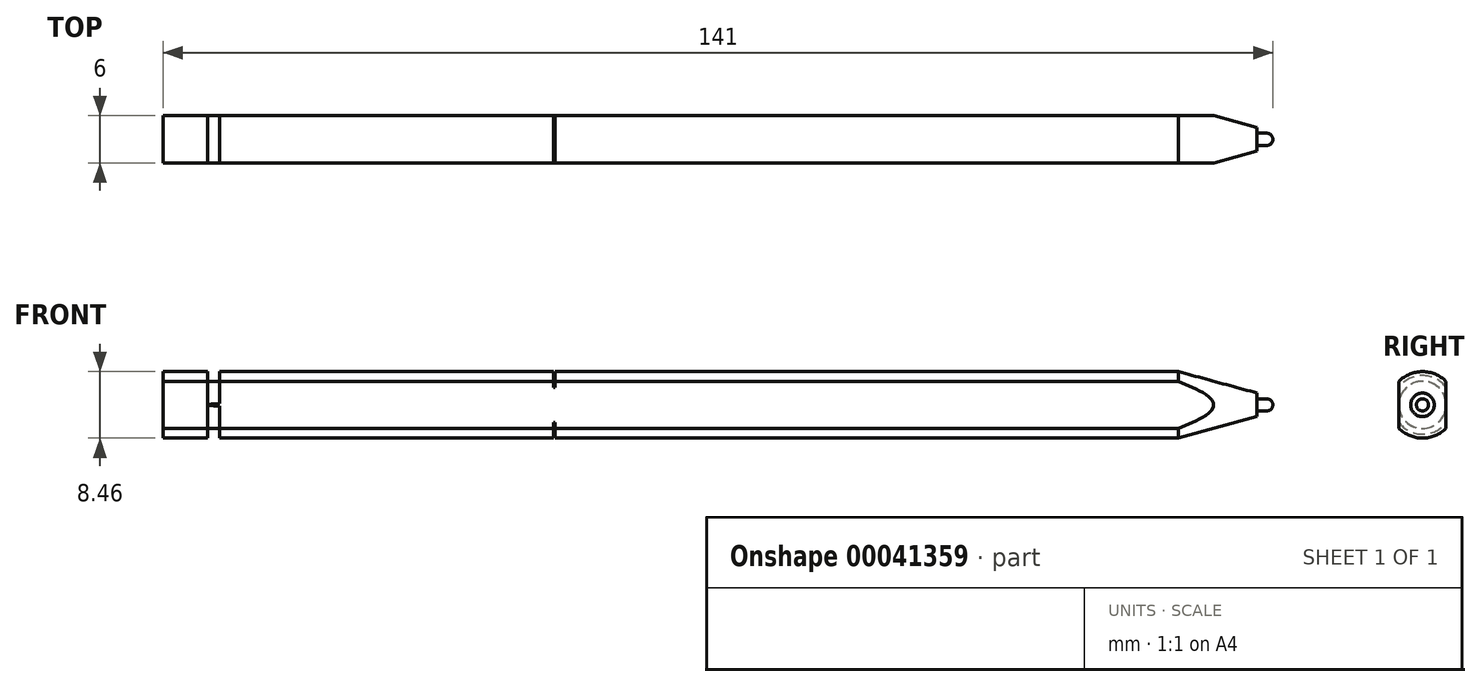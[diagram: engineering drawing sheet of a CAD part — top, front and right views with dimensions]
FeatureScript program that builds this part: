
annotation { "Feature Type Name" : "Feature", "Feature Type Description" : "" }
export const myFeature = defineFeature(function(context is Context, id is Id, definition is map)
    precondition{}
    {
        {
            var Q0;
            Q0=qCreatedBy(makeId("Top.planeOp"),FACE);
            var sketch = newSketch(context, id + "F0", { "sketchPlane" : qUnion([Q0])});
            skLineSegment(sketch, "E0", {"start": v(-68.74, 0) * mm, "end": v(70.26, 0) * mm});
            skLineSegment(sketch, "E1", {"start": v(70.26, 1.5) * mm, "end": v(60.26, 4.22) * mm});
            skLineSegment(sketch, "E2", {"start": v(-63.04, 4.22) * mm, "end": v(-63.04, 3) * mm});
            skLineSegment(sketch, "E3", {"start": v(-63.04, 3) * mm, "end": v(-61.54, 3) * mm});
            skLineSegment(sketch, "E4", {"start": v(-61.54, 3) * mm, "end": v(-61.54, 4.22) * mm});
            skLineSegment(sketch, "E5", {"start": v(-63.04, 4.22) * mm, "end": v(-68.74, 4.22) * mm});
            skLineSegment(sketch, "E6", {"start": v(-68.74, 4.22) * mm, "end": v(-68.74, 0) * mm});
            skLineSegment(sketch, "E7", {"start": v(70.26, 1.5) * mm, "end": v(70.26, 0.78) * mm});
            skPoint(sketch, "E8.orphan", {"position": v(72.26, 0) * mm});
            skLineSegment(sketch, "E9", {"start": v(70.26, 0.78) * mm, "end": v(71.48, 0.78) * mm});
            skArc(sketch, "E10", {"start": v(71.48, 0.78) * mm, "mid": v(72.03, 0.55) * mm, "end": v(72.26, 0) * mm});
            skLineSegment(sketch, "E11", {"start": v(70.26, 0) * mm, "end": v(72.26, 0) * mm});
            skLineSegment(sketch, "E12", {"start": v(-61.54, 4.22) * mm, "end": v(-19.14, 4.22) * mm});
            skLineSegment(sketch, "E13", {"start": v(-18.94, 4.22) * mm, "end": v(-18.94, 3.73) * mm});
            skLineSegment(sketch, "E14", {"start": v(-19.14, 3.73) * mm, "end": v(-18.94, 3.73) * mm});
            skLineSegment(sketch, "E15", {"start": v(-19.14, 3.73) * mm, "end": v(-19.14, 4.22) * mm});
            skLineSegment(sketch, "E16.trimOffspring", {"start": v(-18.94, 4.22) * mm, "end": v(60.26, 4.22) * mm});
            skSolve(sketch);
        }
        {
            var Q0;
            {var subQ0=sQuery(id+"F0.wireOp",EDGE,"E0");Q0=makeQuery(id+"F0.imprint","IMPRINT",FACE,{"disambiguationData":[TD([[makeQuery(id+"F0.imprint","IMPRINT",EDGE,{"derivedFrom":subQ0}),1.0]])]});}
            var Q1;
            Q1=sQuery(id+"F0.wireOp",EDGE,"E0");
            revolve(context, id + "F1", {"entities" : qUnion([Q0]), "axis" : qUnion([Q1]), "revolveType" : RevolveType.FULL});
        }
        {
            var Q0;
            Q0=makeQuery(id+"F1.opRevolve","SWEPT_FACE",FACE,{"disambiguationData":[OSD([sQuery(id+"F0.wireOp",EDGE,"E6")])]});
            var sketch = newSketch(context, id + "F2", { "sketchPlane" : qUnion([Q0])});
            skLineSegment(sketch, "E17.bottom", {"start": v(-3, 4.22) * mm, "end": v(3, 4.22) * mm});
            skLineSegment(sketch, "E17.top", {"start": v(-3, -4.22) * mm, "end": v(3, -4.22) * mm});
            skLineSegment(sketch, "E17.left", {"start": v(-3, 4.22) * mm, "end": v(-3, -4.22) * mm});
            skLineSegment(sketch, "E17.right", {"start": v(3, 4.22) * mm, "end": v(3, -4.22) * mm});
            skSolve(sketch);
        }
        {
            var Q0;
            {var subQ0=makeQuery(id+"F1.opRevolve","SWEPT_EDGE",EDGE,{"disambiguationData":[OSD([sQuery(id+"F0.wireOp",EDGE,"E5"),sQuery(id+"F0.wireOp",EDGE,"E6")])]});var subQ1=sQuery(id+"F2.wireOp",EDGE,"E17.left");var subQ3=makeQuery(id+"F2.imprint","INTERSECT",VERTEX,{"disambiguationData":[OD(0.0)],"derivedFrom":[subQ0,subQ1]});Q0=makeQuery(id+"F2.imprint","IMPRINT",FACE,{"disambiguationData":[TD([[makeQuery(id+"F2.imprint","IMPRINT",EDGE,{"disambiguationData":[TD([[subQ3,-1.0]])],"derivedFrom":subQ1}),-1.0]])]});}
            var Q1;
            {var subQ0=makeQuery(id+"F1.opRevolve","SWEPT_EDGE",EDGE,{"disambiguationData":[OSD([sQuery(id+"F0.wireOp",EDGE,"E5"),sQuery(id+"F0.wireOp",EDGE,"E6")])]});var subQ1=sQuery(id+"F2.wireOp",EDGE,"E17.right");var subQ3=makeQuery(id+"F2.imprint","INTERSECT",VERTEX,{"disambiguationData":[OD(0.0)],"derivedFrom":[subQ0,subQ1]});Q1=makeQuery(id+"F2.imprint","IMPRINT",FACE,{"disambiguationData":[TD([[makeQuery(id+"F2.imprint","IMPRINT",EDGE,{"disambiguationData":[TD([[subQ3,-1.0]])],"derivedFrom":subQ1}),1.0]])]});}
            extrude(context, id + "F3", {"entities" : qUnion([Q0, Q1]), "operationType" : NewBodyOperationType.REMOVE, "endBound" : BoundingType.THROUGH_ALL, "oppositeDirection" : true, "depth" : 25 * mm});
        }
    });
